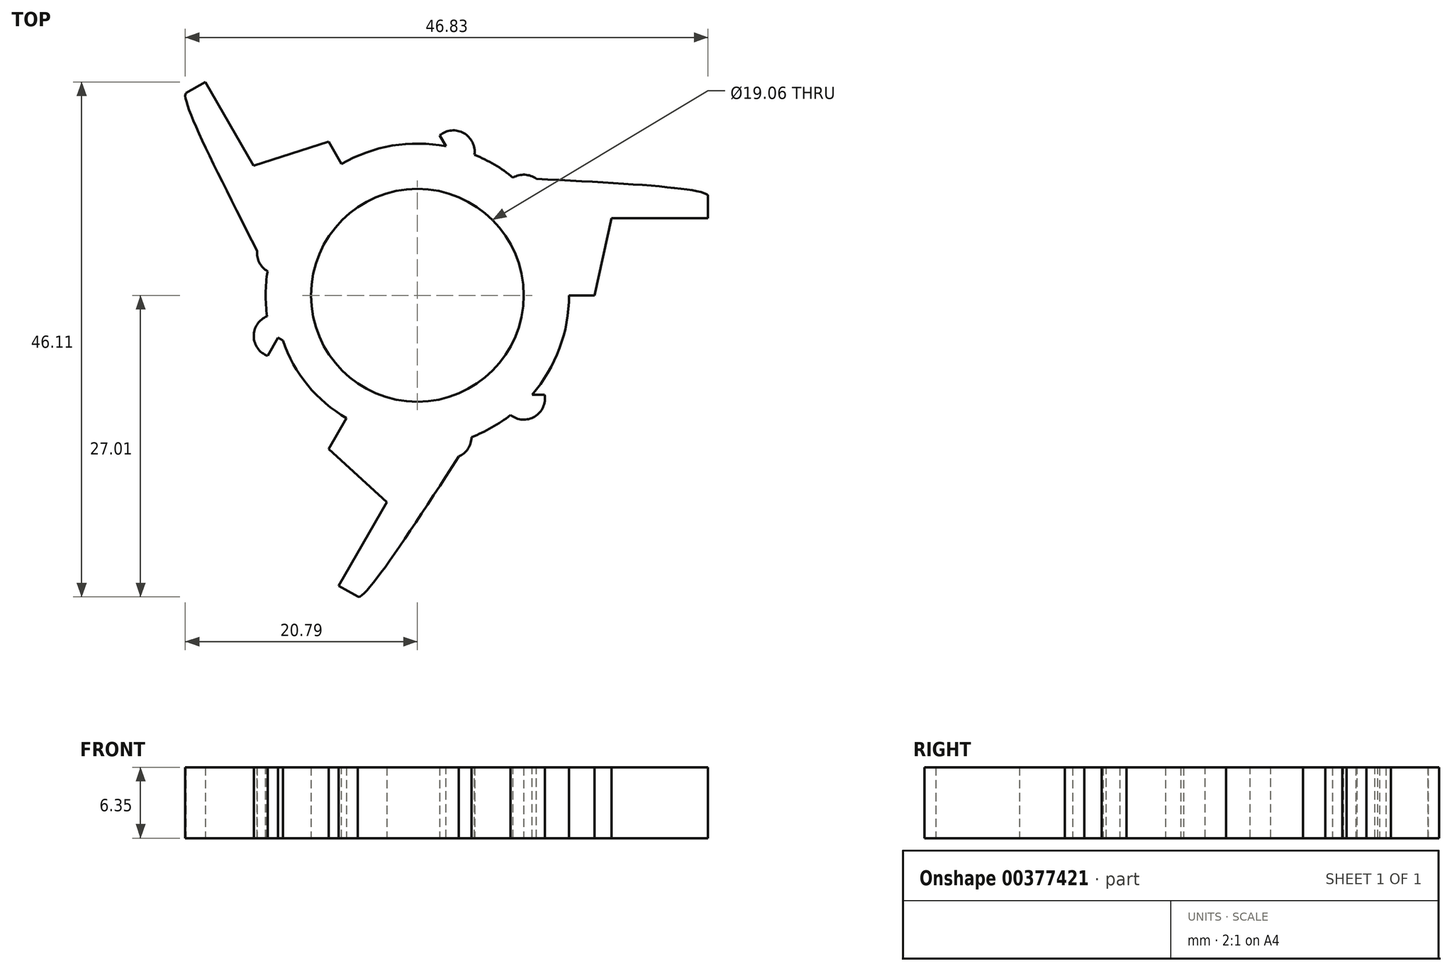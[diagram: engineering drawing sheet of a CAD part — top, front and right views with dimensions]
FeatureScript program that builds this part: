
annotation { "Feature Type Name" : "Feature", "Feature Type Description" : "" }
export const myFeature = defineFeature(function(context is Context, id is Id, definition is map)
    precondition{}
    {
        {
            var Q0;
            Q0=qCreatedBy(makeId("Top.planeOp"),FACE);
            var sketch = newSketch(context, id + "F0", { "sketchPlane" : qUnion([Q0])});
            skCircle(sketch, "E0", {"center": v(0, 0) * mm, "radius": 12.7 * mm});
            skCircle(sketch, "E1", {"center": v(0, 0) * mm, "radius": 9.53 * mm});
            skLineSegment(sketch, "E2", {"start": v(9.53, 0) * mm, "end": v(26.04, 0) * mm});
            skLineSegment(sketch, "E3", {"start": v(26.04, 0) * mm, "end": v(26.04, 8.9) * mm});
            skLineSegment(sketch, "E4", {"start": v(9.53, 0) * mm, "end": v(9.53, -8.9) * mm});
            skLineSegment(sketch, "E5.bottom", {"start": v(9.53, -8.9) * mm, "end": v(26.04, -8.9) * mm});
            skLineSegment(sketch, "E5.top", {"start": v(9.53, 8.9) * mm, "end": v(26.04, 8.9) * mm});
            skLineSegment(sketch, "E5.left", {"start": v(9.53, -8.9) * mm, "end": v(9.53, 8.9) * mm});
            skLineSegment(sketch, "E5.right", {"start": v(26.04, -8.89) * mm, "end": v(26.04, 8.9) * mm});
            skLineSegment(sketch, "E6", {"start": v(26.04, 0) * mm, "end": v(15.88, 0) * mm});
            skPoint(sketch, "E7", {"position": v(26.04, 6.9) * mm});
            skPoint(sketch, "E8", {"position": v(26.04, 0) * mm});
            skPoint(sketch, "E9", {"position": v(26.04, -6.9) * mm});
            skLineSegment(sketch, "E10", {"start": v(26.04, -6.9) * mm, "end": v(17.4, -6.9) * mm});
            skLineSegment(sketch, "E11", {"start": v(26.04, 6.9) * mm, "end": v(17.4, 6.9) * mm});
            skLineSegment(sketch, "E12", {"start": v(17.4, 6.9) * mm, "end": v(15.88, 0) * mm});
            skLineSegment(sketch, "E13", {"start": v(17.4, -6.9) * mm, "end": v(15.88, 0) * mm});
            skCircle(sketch, "E14", {"center": v(9.53, 8.9) * mm, "radius": 1.9 * mm});
            skCircle(sketch, "E15", {"center": v(9.53, -9.23) * mm, "radius": 1.9 * mm});
            skSolve(sketch);
        }
        {
            var Q0;
            {var subQ0=sQuery(id+"F0.wireOp",EDGE,"E14");var subQ1=sQuery(id+"F0.wireOp",EDGE,"E0");var subQ2=makeQuery(id+"F0.imprint","INTERSECT",VERTEX,{"disambiguationData":[OD(1.0)],"derivedFrom":[subQ1,subQ0]});Q0=makeQuery(id+"F0.imprint","IMPRINT",FACE,{"disambiguationData":[TD([[makeQuery(id+"F0.imprint","IMPRINT",EDGE,{"disambiguationData":[TD([[subQ2,1.0]])],"derivedFrom":subQ1}),1.0]])]});}
            var Q1;
            {var subQ0=sQuery(id+"F0.wireOp",EDGE,"E5.left");var subQ1=sQuery(id+"F0.wireOp",EDGE,"E0");var subQ2=makeQuery(id+"F0.imprint","INTERSECT",VERTEX,{"disambiguationData":[OD(1.0)],"derivedFrom":[subQ1,subQ0]});Q1=makeQuery(id+"F0.imprint","IMPRINT",FACE,{"disambiguationData":[TD([[makeQuery(id+"F0.imprint","IMPRINT",EDGE,{"disambiguationData":[TD([[subQ2,-1.0]])],"derivedFrom":subQ1}),1.0]])]});}
            var Q2;
            {var subQ0=sQuery(id+"F0.wireOp",EDGE,"E5.left");var subQ1=sQuery(id+"F0.wireOp",EDGE,"E0");var subQ2=makeQuery(id+"F0.imprint","INTERSECT",VERTEX,{"disambiguationData":[OD(1.0)],"derivedFrom":[subQ1,subQ0]});Q2=makeQuery(id+"F0.imprint","IMPRINT",FACE,{"disambiguationData":[TD([[makeQuery(id+"F0.imprint","IMPRINT",EDGE,{"disambiguationData":[TD([[subQ2,-1.0]])],"derivedFrom":subQ1}),-1.0]])]});}
            var Q3;
            {var subQ0=sQuery(id+"F0.wireOp",EDGE,"E15");var subQ1=sQuery(id+"F0.wireOp",EDGE,"E0");var subQ2=makeQuery(id+"F0.imprint","INTERSECT",VERTEX,{"disambiguationData":[OD(0.0)],"derivedFrom":[subQ1,subQ0]});Q3=makeQuery(id+"F0.imprint","IMPRINT",FACE,{"disambiguationData":[TD([[makeQuery(id+"F0.imprint","IMPRINT",EDGE,{"disambiguationData":[TD([[subQ2,-1.0]])],"derivedFrom":subQ1}),1.0]])]});}
            var Q4;
            {var subQ0=sQuery(id+"F0.wireOp",EDGE,"E14");var subQ1=sQuery(id+"F0.wireOp",EDGE,"E0");var subQ2=makeQuery(id+"F0.imprint","INTERSECT",VERTEX,{"disambiguationData":[OD(0.0)],"derivedFrom":[subQ1,subQ0]});Q4=makeQuery(id+"F0.imprint","IMPRINT",FACE,{"disambiguationData":[TD([[makeQuery(id+"F0.imprint","IMPRINT",EDGE,{"disambiguationData":[TD([[subQ2,1.0]])],"derivedFrom":subQ1}),1.0]])]});}
            var Q5;
            {var subQ3=sQuery(id+"F0.wireOp",EDGE,"E11");Q5=makeQuery(id+"F0.imprint","IMPRINT",FACE,{"disambiguationData":[TD([[makeQuery(id+"F0.imprint","IMPRINT",EDGE,{"derivedFrom":subQ3}),-1.0]])]});}
            var Q6;
            {var subQ0=sQuery(id+"F0.wireOp",EDGE,"E14");var subQ1=sQuery(id+"F0.wireOp",EDGE,"E0");var subQ2=makeQuery(id+"F0.imprint","INTERSECT",VERTEX,{"disambiguationData":[OD(1.0)],"derivedFrom":[subQ1,subQ0]});Q6=makeQuery(id+"F0.imprint","IMPRINT",FACE,{"disambiguationData":[TD([[makeQuery(id+"F0.imprint","IMPRINT",EDGE,{"disambiguationData":[TD([[subQ2,-1.0]])],"derivedFrom":subQ1}),1.0]])]});}
            var Q7;
            {var subQ0=sQuery(id+"F0.wireOp",EDGE,"E14");var subQ1=sQuery(id+"F0.wireOp",EDGE,"E0");var subQ2=makeQuery(id+"F0.imprint","INTERSECT",VERTEX,{"disambiguationData":[OD(1.0)],"derivedFrom":[subQ1,subQ0]});Q7=makeQuery(id+"F0.imprint","IMPRINT",FACE,{"disambiguationData":[TD([[makeQuery(id+"F0.imprint","IMPRINT",EDGE,{"disambiguationData":[TD([[subQ2,-1.0]])],"derivedFrom":subQ1}),-1.0]])]});}
            var Q8;
            {var subQ0=sQuery(id+"F0.wireOp",EDGE,"E15");var subQ1=sQuery(id+"F0.wireOp",EDGE,"E0");var subQ2=makeQuery(id+"F0.imprint","INTERSECT",VERTEX,{"disambiguationData":[OD(0.0)],"derivedFrom":[subQ1,subQ0]});Q8=makeQuery(id+"F0.imprint","IMPRINT",FACE,{"disambiguationData":[TD([[makeQuery(id+"F0.imprint","IMPRINT",EDGE,{"disambiguationData":[TD([[subQ2,-1.0]])],"derivedFrom":subQ1}),-1.0]])]});}
            var Q9;
            {var subQ0=sQuery(id+"F0.wireOp",EDGE,"E14");var subQ1=sQuery(id+"F0.wireOp",EDGE,"E0");var subQ2=makeQuery(id+"F0.imprint","INTERSECT",VERTEX,{"disambiguationData":[OD(0.0)],"derivedFrom":[subQ1,subQ0]});Q9=makeQuery(id+"F0.imprint","IMPRINT",FACE,{"disambiguationData":[TD([[makeQuery(id+"F0.imprint","IMPRINT",EDGE,{"disambiguationData":[TD([[subQ2,1.0]])],"derivedFrom":subQ1}),-1.0]])]});}
            var Q10;
            {var subQ3=sQuery(id+"F0.wireOp",EDGE,"E10");Q10=makeQuery(id+"F0.imprint","IMPRINT",FACE,{"disambiguationData":[TD([[makeQuery(id+"F0.imprint","IMPRINT",EDGE,{"derivedFrom":subQ3}),1.0]])]});}
            var Q11;
            {var subQ0=sQuery(id+"F0.wireOp",EDGE,"E2");var subQ1=sQuery(id+"F0.wireOp",EDGE,"E0");var subQ2=makeQuery(id+"F0.imprint","INTERSECT",VERTEX,{"derivedFrom":[subQ1,subQ0]});Q11=makeQuery(id+"F0.imprint","IMPRINT",FACE,{"disambiguationData":[TD([[makeQuery(id+"F0.imprint","IMPRINT",EDGE,{"disambiguationData":[TD([[subQ2,1.0]])],"derivedFrom":subQ1}),1.0]])]});}
            var Q12;
            {var subQ1=sQuery(id+"F0.wireOp",EDGE,"E1");Q12=makeQuery(id+"F0.imprint","IMPRINT",FACE,{"disambiguationData":[TD([[makeQuery(id+"F0.imprint","IMPRINT",EDGE,{"derivedFrom":subQ1}),-1.0]])]});}
            extrude(context, id + "F1", {"entities" : qUnion([Q0, Q1, Q2, Q3, Q4, Q5, Q6, Q7, Q8, Q9, Q10, Q11, Q12]), "depth" : 6.35 * mm});
        }
        {
            var Q0;
            Q0=qCreatedBy(makeId("Front.planeOp"),FACE);
            var sketch = newSketch(context, id + "F2", { "sketchPlane" : qUnion([Q0])});
            skLineSegment(sketch, "E16", {"start": v(0, 0) * mm, "end": v(0, 6.35) * mm});
            skSolve(sketch);
        }
        {
            var Q0;
            Q0=makeQuery(id+"F1.opExtrude","SWEPT_BODY",BODY,{"disambiguationData":[OSD([sQuery(id+"F0.wireOp",EDGE,"E0"),sQuery(id+"F0.wireOp",EDGE,"E1"),sQuery(id+"F0.wireOp",EDGE,"E5.bottom"),sQuery(id+"F0.wireOp",EDGE,"E5.top"),sQuery(id+"F0.wireOp",EDGE,"E5.right"),sQuery(id+"F0.wireOp",EDGE,"E10"),sQuery(id+"F0.wireOp",EDGE,"E11"),sQuery(id+"F0.wireOp",EDGE,"E12"),sQuery(id+"F0.wireOp",EDGE,"E13"),sQuery(id+"F0.wireOp",EDGE,"E14"),sQuery(id+"F0.wireOp",EDGE,"E15")])]});
            var Q1;
            Q1=sQuery(id+"F2.wireOp",EDGE,"E16");
            circularPattern(context, id + "F3", {"entities" : qUnion([Q0]), "axis" : qUnion([Q1]), "angle" : 360 * degree, "instanceCount" : 3, "equalSpace" : true});
        }
        {
            var Q0;
            Q0=makeQuery(id+"F3.opPattern","COPY",FACE,{"derivedFrom":makeQuery(id+"F1.opExtrude","CAP_FACE",FACE,{"disambiguationData":[OSD([sQuery(id+"F0.wireOp",EDGE,"E0"),sQuery(id+"F0.wireOp",EDGE,"E1"),sQuery(id+"F0.wireOp",EDGE,"E5.bottom"),sQuery(id+"F0.wireOp",EDGE,"E5.top"),sQuery(id+"F0.wireOp",EDGE,"E5.right"),sQuery(id+"F0.wireOp",EDGE,"E10"),sQuery(id+"F0.wireOp",EDGE,"E11"),sQuery(id+"F0.wireOp",EDGE,"E12"),sQuery(id+"F0.wireOp",EDGE,"E13"),sQuery(id+"F0.wireOp",EDGE,"E14"),sQuery(id+"F0.wireOp",EDGE,"E15")])],"isStart":false}),"instanceName":"2"});
            var sketch = newSketch(context, id + "F4", { "sketchPlane" : qUnion([Q0])});
            skCircle(sketch, "E17", {"center": v(0, 0) * mm, "radius": 13.59 * mm});
            skSolve(sketch);
        }
        {
            var Q0;
            {var subQ5=makeQuery(id+"F3.opPattern","COPY",EDGE,{"derivedFrom":makeQuery(id+"F1.opExtrude","CAP_EDGE",EDGE,{"disambiguationData":[OSD([sQuery(id+"F0.wireOp",EDGE,"E0")])],"isStart":false}),"instanceName":"2"});Q0=makeQuery(id+"F4.imprint","IMPRINT",FACE,{"disambiguationData":[TD([[makeQuery(id+"F4.imprint","IMPRINT",EDGE,{"derivedFrom":subQ5}),-1.0]])]});}
            var Q1;
            {var subQ1=makeQuery(id+"F3.opPattern","COPY",EDGE,{"derivedFrom":makeQuery(id+"F1.opExtrude","CAP_EDGE",EDGE,{"disambiguationData":[OSD([sQuery(id+"F0.wireOp",EDGE,"E0")])],"isStart":false}),"instanceName":"2"});Q1=makeQuery(id+"F4.imprint","IMPRINT",FACE,{"disambiguationData":[TD([[makeQuery(id+"F4.imprint","IMPRINT",EDGE,{"derivedFrom":subQ1}),1.0]])]});}
            extrude(context, id + "F5", {"entities" : qUnion([Q0, Q1]), "operationType" : NewBodyOperationType.ADD, "oppositeDirection" : true, "depth" : 6.35 * mm});
        }
        {
            var Q0;
            {var subQ0=sQuery(id+"F0.wireOp",EDGE,"E1");var subQ1=makeQuery(id+"F1.opExtrude","CAP_FACE",FACE,{"disambiguationData":[OSD([sQuery(id+"F0.wireOp",EDGE,"E0"),subQ0,sQuery(id+"F0.wireOp",EDGE,"E5.bottom"),sQuery(id+"F0.wireOp",EDGE,"E5.top"),sQuery(id+"F0.wireOp",EDGE,"E5.right"),sQuery(id+"F0.wireOp",EDGE,"E10"),sQuery(id+"F0.wireOp",EDGE,"E11"),sQuery(id+"F0.wireOp",EDGE,"E12"),sQuery(id+"F0.wireOp",EDGE,"E13"),sQuery(id+"F0.wireOp",EDGE,"E14"),sQuery(id+"F0.wireOp",EDGE,"E15")])],"isStart":false});Q0=makeQuery(id+"F5.boolean.opBoolean","MERGE",FACE,{"derivedFrom":[subQ1,makeQuery(id+"F3.opPattern","COPY",FACE,{"derivedFrom":subQ1,"instanceName":"1"}),makeQuery(id+"F3.opPattern","COPY",FACE,{"derivedFrom":subQ1,"instanceName":"2"}),makeQuery(id+"F5.opExtrude","CAP_FACE",FACE,{"disambiguationData":[OSD([subQ0,sQuery(id+"F4.wireOp",EDGE,"E17")])],"isStart":true})]});}
            var sketch = newSketch(context, id + "F6", { "sketchPlane" : qUnion([Q0])});
            skFitSpline(sketch, "E18", {"points": [v(8.58, 10.54) * mm, v(26.04, 8.9) * mm, v(17.4, 6.9) * mm], "startDerivative": vector(44.67, -2.26) * mm, "endDerivative": vector(-31.3, -5.17) * mm});
            skFitSpline(sketch, "E19", {"points": [v(5.12, 12.59) * mm, v(-5.32, 27) * mm, v(-2.72, 18.52) * mm], "startDerivative": vector(-24.87, 37.77) * mm, "endDerivative": vector(11.27, -29.79) * mm});
            skFitSpline(sketch, "E20", {"points": [v(-13.42, 2.16) * mm, v(-20.72, 18.1) * mm, v(-14.68, 11.61) * mm], "startDerivative": vector(-20.38, 39.82) * mm, "endDerivative": vector(20.13, -24.53) * mm});
            skFitSpline(sketch, "E21", {"points": [v(-13.46, -1.86) * mm, v(-20.72, -18.1) * mm, v(-14.68, -11.61) * mm], "startDerivative": vector(-20.28, -40.42) * mm, "endDerivative": vector(20.16, 24.66) * mm});
            skFitSpline(sketch, "E22", {"points": [v(4.84, -12.7) * mm, v(-5.32, -27) * mm, v(-2.72, -18.52) * mm], "startDerivative": vector(-24.3, -37.56) * mm, "endDerivative": vector(11.18, 29.7) * mm});
            skFitSpline(sketch, "E23", {"points": [v(8.34, -10.73) * mm, v(26.04, -8.9) * mm, v(17.4, -6.9) * mm], "startDerivative": vector(45.14, 2.65) * mm, "endDerivative": vector(-31.43, 5.13) * mm});
            skSolve(sketch);
        }
        {
            var Q0;
            {var subQ2=sQuery(id+"F0.wireOp",EDGE,"E5.bottom");var subQ3=makeQuery(id+"F3.opPattern","COPY",EDGE,{"derivedFrom":makeQuery(id+"F1.opExtrude","CAP_EDGE",EDGE,{"disambiguationData":[OSD([subQ2])],"isStart":false}),"instanceName":"1"});Q0=makeQuery(id+"F6.imprint","IMPRINT",FACE,{"disambiguationData":[TD([[makeQuery(id+"F6.imprint","IMPRINT",EDGE,{"derivedFrom":subQ3}),-1.0]])]});}
            var Q1;
            {var subQ2=sQuery(id+"F0.wireOp",EDGE,"E5.top");var subQ3=makeQuery(id+"F1.opExtrude","CAP_EDGE",EDGE,{"disambiguationData":[OSD([subQ2])],"isStart":false});Q1=makeQuery(id+"F6.imprint","IMPRINT",FACE,{"disambiguationData":[TD([[makeQuery(id+"F6.imprint","IMPRINT",EDGE,{"derivedFrom":subQ3}),1.0]])]});}
            var Q2;
            {var subQ2=sQuery(id+"F0.wireOp",EDGE,"E5.bottom");var subQ3=makeQuery(id+"F1.opExtrude","CAP_EDGE",EDGE,{"disambiguationData":[OSD([subQ2])],"isStart":false});Q2=makeQuery(id+"F6.imprint","IMPRINT",FACE,{"disambiguationData":[TD([[makeQuery(id+"F6.imprint","IMPRINT",EDGE,{"derivedFrom":subQ3}),-1.0]])]});}
            var Q3;
            {var subQ2=sQuery(id+"F0.wireOp",EDGE,"E5.top");var subQ3=makeQuery(id+"F3.opPattern","COPY",EDGE,{"derivedFrom":makeQuery(id+"F1.opExtrude","CAP_EDGE",EDGE,{"disambiguationData":[OSD([subQ2])],"isStart":false}),"instanceName":"2"});Q3=makeQuery(id+"F6.imprint","IMPRINT",FACE,{"disambiguationData":[TD([[makeQuery(id+"F6.imprint","IMPRINT",EDGE,{"derivedFrom":subQ3}),1.0]])]});}
            var Q4;
            {var subQ2=sQuery(id+"F0.wireOp",EDGE,"E5.bottom");var subQ3=makeQuery(id+"F3.opPattern","COPY",EDGE,{"derivedFrom":makeQuery(id+"F1.opExtrude","CAP_EDGE",EDGE,{"disambiguationData":[OSD([subQ2])],"isStart":false}),"instanceName":"2"});Q4=makeQuery(id+"F6.imprint","IMPRINT",FACE,{"disambiguationData":[TD([[makeQuery(id+"F6.imprint","IMPRINT",EDGE,{"derivedFrom":subQ3}),-1.0]])]});}
            var Q5;
            {var subQ2=sQuery(id+"F0.wireOp",EDGE,"E5.top");var subQ3=makeQuery(id+"F3.opPattern","COPY",EDGE,{"derivedFrom":makeQuery(id+"F1.opExtrude","CAP_EDGE",EDGE,{"disambiguationData":[OSD([subQ2])],"isStart":false}),"instanceName":"1"});Q5=makeQuery(id+"F6.imprint","IMPRINT",FACE,{"disambiguationData":[TD([[makeQuery(id+"F6.imprint","IMPRINT",EDGE,{"derivedFrom":subQ3}),1.0]])]});}
            extrude(context, id + "F7", {"entities" : qUnion([Q0, Q1, Q2, Q3, Q4, Q5]), "operationType" : NewBodyOperationType.ADD, "oppositeDirection" : true, "depth" : 6.35 * mm});
        }
    });
